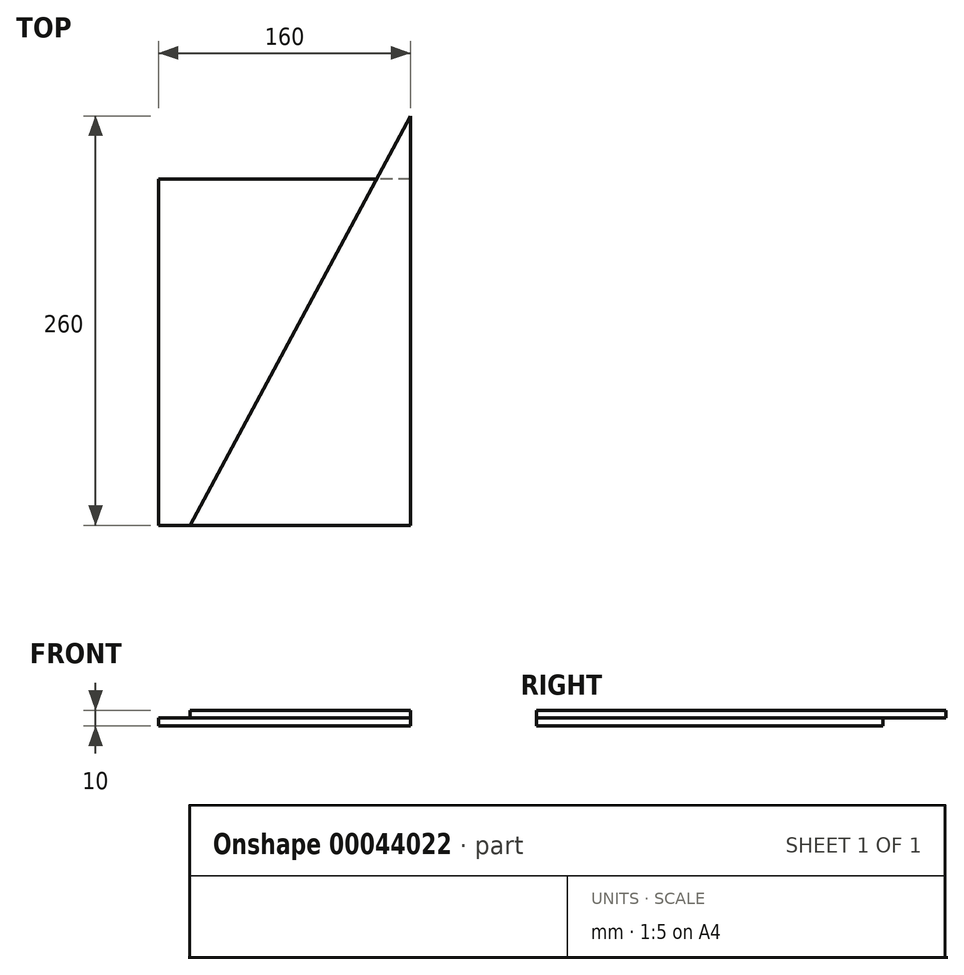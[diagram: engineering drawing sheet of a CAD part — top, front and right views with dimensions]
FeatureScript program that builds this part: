
annotation { "Feature Type Name" : "Feature", "Feature Type Description" : "" }
export const myFeature = defineFeature(function(context is Context, id is Id, definition is map)
    precondition{}
    {
        {
            var Q0;
            Q0=qCreatedBy(makeId("Top.planeOp"),FACE);
            var sketch = newSketch(context, id + "F0", { "sketchPlane" : qUnion([Q0])});
            skLineSegment(sketch, "E0.rect.bottom", {"start": v(80, 110) * mm, "end": v(-80, 110) * mm});
            skLineSegment(sketch, "E0.rect.top", {"start": v(80, -110) * mm, "end": v(-80, -110) * mm});
            skLineSegment(sketch, "E0.rect.left", {"start": v(80, 110) * mm, "end": v(80, -110) * mm});
            skLineSegment(sketch, "E0.rect.right", {"start": v(-80, 110) * mm, "end": v(-80, -110) * mm});
            skPoint(sketch, "E0.rect.middle", {"position": v(0, 0) * mm});
            skSolve(sketch);
        }
        {
            var Q0;
            Q0=makeQuery(id+"F0.imprint","IMPRINT",FACE,{"disambiguationData":[TD([[makeQuery(id+"F0.imprint","IMPRINT",EDGE,{"derivedFrom":sQuery(id+"F0.wireOp",EDGE,"E0.rect.bottom")}),1.0]])]});
            extrude(context, id + "F1", {"entities" : qUnion([Q0]), "depth" : 5 * mm});
        }
        {
            var Q0;
            Q0=makeQuery(id+"F1.opExtrude","CAP_FACE",FACE,{"disambiguationData":[OSD([sQuery(id+"F0.wireOp",EDGE,"E0.rect.bottom"),sQuery(id+"F0.wireOp",EDGE,"E0.rect.top"),sQuery(id+"F0.wireOp",EDGE,"E0.rect.left"),sQuery(id+"F0.wireOp",EDGE,"E0.rect.right")])],"isStart":false});
            var sketch = newSketch(context, id + "F2", { "sketchPlane" : qUnion([Q0])});
            skLineSegment(sketch, "E1.bottom", {"start": v(80, -110) * mm, "end": v(-60, -110) * mm});
            skLineSegment(sketch, "E1.left", {"start": v(80, -110) * mm, "end": v(80, 150) * mm});
            skLineSegment(sketch, "E2", {"start": v(-60, -110) * mm, "end": v(80, 150) * mm});
            skSolve(sketch);
        }
        {
            var Q0;
            Q0 = qSketchRegion(id + "F2", true);
            extrude(context, id + "F3", {"entities" : qUnion([Q0]), "depth" : 5 * mm});
        }
    });
